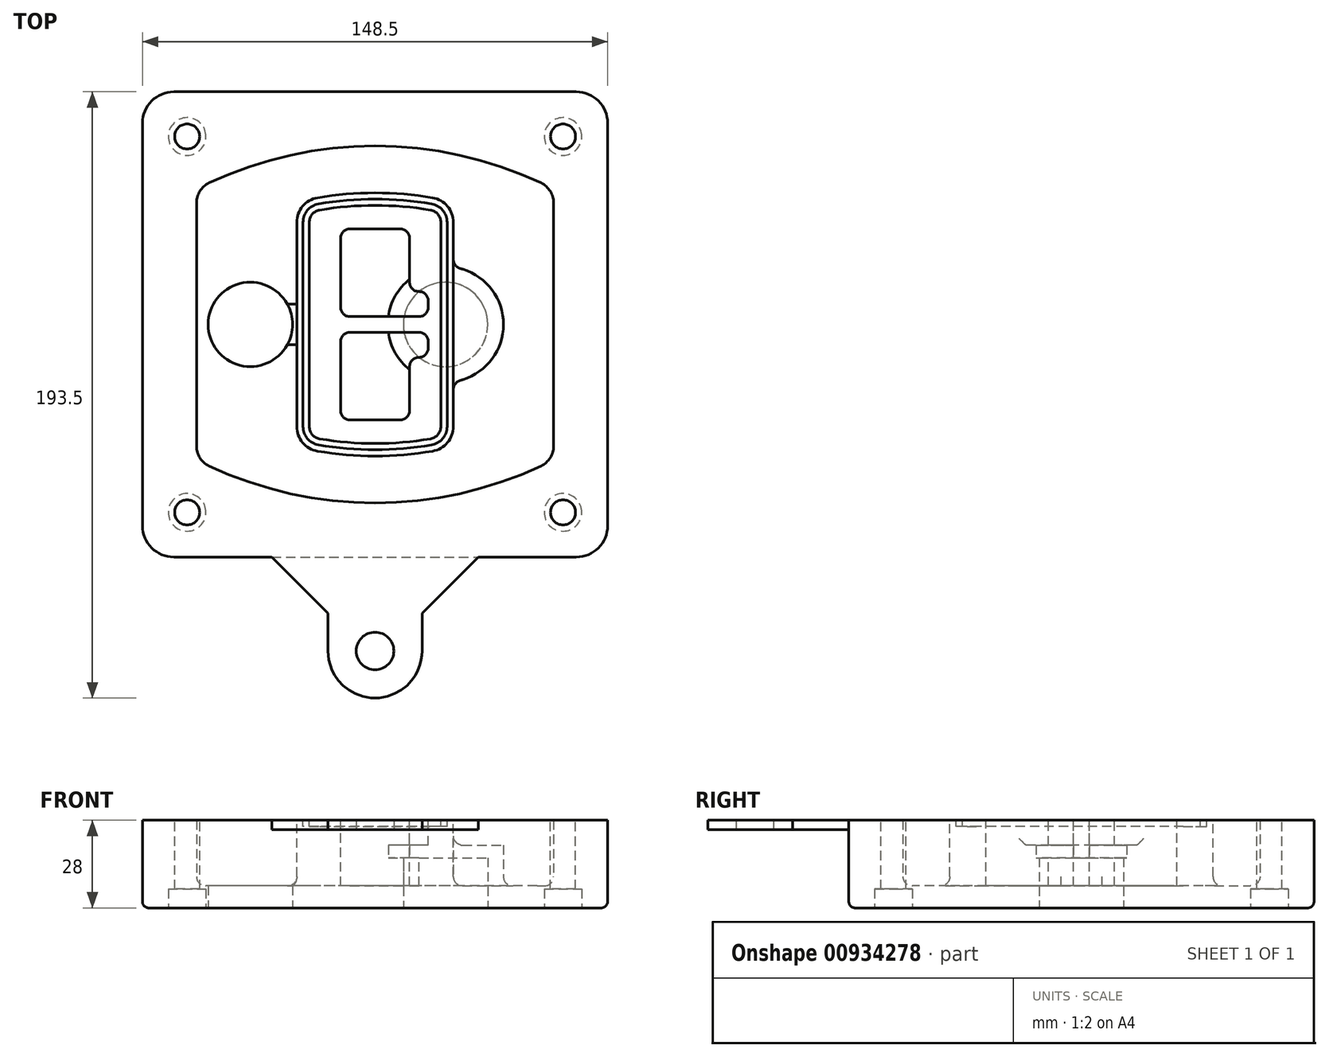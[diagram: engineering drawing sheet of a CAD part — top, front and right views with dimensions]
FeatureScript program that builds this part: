
annotation { "Feature Type Name" : "Feature", "Feature Type Description" : "" }
export const myFeature = defineFeature(function(context is Context, id is Id, definition is map)
    precondition{}
    {
        {
            var Q0;
            Q0=qCreatedBy(makeId("Top.planeOp"),FACE);
            var sketch = newSketch(context, id + "F0", { "sketchPlane" : qUnion([Q0])});
            skPoint(sketch, "E0.rect.middle", {"position": v(0, 0) * mm});
            skLineSegment(sketch, "E1.bottom", {"start": v(-64.25, -74.25) * mm, "end": v(64.25, -74.25) * mm});
            skLineSegment(sketch, "E1.top", {"start": v(-64.25, 74.25) * mm, "end": v(64.25, 74.25) * mm});
            skLineSegment(sketch, "E1.left", {"start": v(-74.25, -64.25) * mm, "end": v(-74.25, 64.25) * mm});
            skLineSegment(sketch, "E1.right", {"start": v(74.25, -64.25) * mm, "end": v(74.25, 64.25) * mm});
            skLineSegment(sketch, "E2", {"start": v(-74.25, 74.25) * mm, "end": v(74.25, -74.25) * mm, "construction": true});
            skLineSegment(sketch, "E3", {"start": v(74.25, 74.25) * mm, "end": v(-74.25, -74.25) * mm, "construction": true});
            skCircle(sketch, "E4", {"center": v(-60, 60) * mm, "radius": 4 * mm});
            skCircle(sketch, "E5", {"center": v(60, 60) * mm, "radius": 4 * mm});
            skCircle(sketch, "E6", {"center": v(60, -60) * mm, "radius": 4 * mm});
            skCircle(sketch, "E7", {"center": v(-60, -60) * mm, "radius": 4 * mm});
            skLineSegment(sketch, "E8", {"start": v(-60, 60) * mm, "end": v(60, 60) * mm, "construction": true});
            skLineSegment(sketch, "E9", {"start": v(60, 60) * mm, "end": v(60, -60) * mm, "construction": true});
            skLineSegment(sketch, "E10", {"start": v(60, -60) * mm, "end": v(-60, -60) * mm, "construction": true});
            skLineSegment(sketch, "E11", {"start": v(-60, -60) * mm, "end": v(-60, 60) * mm, "construction": true});
            skLineSegment(sketch, "E12", {"start": v(-60, 38.83) * mm, "end": v(-60, -38.83) * mm});
            skLineSegment(sketch, "E13", {"start": v(60, 38.83) * mm, "end": v(60, -38.83) * mm});
            skArc(sketch, "E14", {"start": v(54.26, 47.88) * mm, "mid": v(0, 60) * mm, "end": v(-54.26, 47.88) * mm});
            skArc(sketch, "E15", {"start": v(-54.26, -47.88) * mm, "mid": v(0, -60) * mm, "end": v(54.26, -47.88) * mm});
            skLineSegment(sketch, "E16", {"start": v(-60, 0) * mm, "end": v(60, 0) * mm, "construction": true});
            skPoint(sketch, "E17.visualSharp", {"position": v(-60, -45) * mm});
            skArc(sketch, "E17.filletArc", {"start": v(-60, -38.83) * mm, "mid": v(-58.44, -44.2) * mm, "end": v(-54.26, -47.88) * mm});
            skPoint(sketch, "E18.visualSharp", {"position": v(-60, 45) * mm});
            skArc(sketch, "E18.filletArc", {"start": v(-54.26, 47.88) * mm, "mid": v(-58.44, 44.2) * mm, "end": v(-60, 38.83) * mm});
            skPoint(sketch, "E19.visualSharp", {"position": v(60, 45) * mm});
            skArc(sketch, "E19.filletArc", {"start": v(60, 38.83) * mm, "mid": v(58.44, 44.2) * mm, "end": v(54.26, 47.88) * mm});
            skPoint(sketch, "E20.visualSharp", {"position": v(60, -45) * mm});
            skArc(sketch, "E20.filletArc", {"start": v(54.26, -47.88) * mm, "mid": v(58.44, -44.2) * mm, "end": v(60, -38.83) * mm});
            skPoint(sketch, "E21.visualSharp", {"position": v(-74.25, 74.25) * mm});
            skArc(sketch, "E21.filletArc", {"start": v(-64.25, 74.25) * mm, "mid": v(-71.32, 71.32) * mm, "end": v(-74.25, 64.25) * mm});
            skPoint(sketch, "E22.visualSharp", {"position": v(74.25, 74.25) * mm});
            skArc(sketch, "E22.filletArc", {"start": v(74.25, 64.25) * mm, "mid": v(71.32, 71.32) * mm, "end": v(64.25, 74.25) * mm});
            skPoint(sketch, "E23.visualSharp", {"position": v(74.25, -74.25) * mm});
            skArc(sketch, "E23.filletArc", {"start": v(64.25, -74.25) * mm, "mid": v(71.32, -71.32) * mm, "end": v(74.25, -64.25) * mm});
            skPoint(sketch, "E24.visualSharp", {"position": v(-74.25, -74.25) * mm});
            skArc(sketch, "E24.filletArc", {"start": v(-74.25, -64.25) * mm, "mid": v(-71.32, -71.32) * mm, "end": v(-64.25, -74.25) * mm});
            skArc(sketch, "E25.0", {"start": v(57, 38.83) * mm, "mid": v(55.9, 42.58) * mm, "end": v(52.98, 45.17) * mm});
            skLineSegment(sketch, "E25.1", {"start": v(57, 38.83) * mm, "end": v(57, -38.83) * mm});
            skArc(sketch, "E25.2", {"start": v(52.98, -45.17) * mm, "mid": v(55.9, -42.58) * mm, "end": v(57, -38.83) * mm});
            skArc(sketch, "E25.3", {"start": v(-52.98, -45.17) * mm, "mid": v(0, -57) * mm, "end": v(52.98, -45.17) * mm});
            skArc(sketch, "E25.4", {"start": v(-57, -38.83) * mm, "mid": v(-55.9, -42.58) * mm, "end": v(-52.98, -45.17) * mm});
            skArc(sketch, "E25.5", {"start": v(52.98, 45.17) * mm, "mid": v(0, 57) * mm, "end": v(-52.98, 45.17) * mm});
            skLineSegment(sketch, "E25.6", {"start": v(-57, 38.83) * mm, "end": v(-57, -38.83) * mm});
            skArc(sketch, "E25.7", {"start": v(-52.98, 45.17) * mm, "mid": v(-55.9, 42.58) * mm, "end": v(-57, 38.83) * mm});
            skArc(sketch, "E26.0", {"start": v(-55.96, 51.5) * mm, "mid": v(-61.82, 46.33) * mm, "end": v(-64, 38.83) * mm});
            skArc(sketch, "E26.1", {"start": v(55.96, 51.5) * mm, "mid": v(0, 64) * mm, "end": v(-55.96, 51.5) * mm});
            skArc(sketch, "E26.2", {"start": v(64, 38.83) * mm, "mid": v(61.82, 46.33) * mm, "end": v(55.96, 51.5) * mm});
            skLineSegment(sketch, "E26.3", {"start": v(64, 38.83) * mm, "end": v(64, -38.83) * mm});
            skArc(sketch, "E26.4", {"start": v(55.96, -51.5) * mm, "mid": v(61.82, -46.33) * mm, "end": v(64, -38.83) * mm});
            skLineSegment(sketch, "E26.5", {"start": v(-64, 38.83) * mm, "end": v(-64, -38.83) * mm});
            skArc(sketch, "E26.6", {"start": v(-55.96, -51.5) * mm, "mid": v(0, -64) * mm, "end": v(55.96, -51.5) * mm});
            skArc(sketch, "E26.7", {"start": v(-64, -38.83) * mm, "mid": v(-61.82, -46.33) * mm, "end": v(-55.96, -51.5) * mm});
            skSolve(sketch);
        }
        {
            var Q0;
            Q0=makeQuery(id+"F0.imprint","IMPRINT",FACE,{"disambiguationData":[TD([[makeQuery(id+"F0.imprint","IMPRINT",EDGE,{"derivedFrom":sQuery(id+"F0.wireOp",EDGE,"E1.bottom")}),1.0]])]});
            var Q1;
            Q1=makeQuery(id+"F0.imprint","IMPRINT",FACE,{"disambiguationData":[TD([[makeQuery(id+"F0.imprint","IMPRINT",EDGE,{"derivedFrom":sQuery(id+"F0.wireOp",EDGE,"E12")}),1.0]])]});
            var Q2;
            Q2=makeQuery(id+"F0.imprint","IMPRINT",FACE,{"disambiguationData":[TD([[makeQuery(id+"F0.imprint","IMPRINT",EDGE,{"derivedFrom":sQuery(id+"F0.wireOp",EDGE,"E25.0")}),1.0]])]});
            var Q3;
            Q3=makeQuery(id+"F0.imprint","IMPRINT",FACE,{"disambiguationData":[TD([[makeQuery(id+"F0.imprint","IMPRINT",EDGE,{"derivedFrom":sQuery(id+"F0.wireOp",EDGE,"E12")}),-1.0]])]});
            extrude(context, id + "F1", {"entities" : qUnion([Q0, Q1, Q2, Q3]), "oppositeDirection" : true, "depth" : 25 * mm});
        }
        {
            var Q0;
            Q0=makeQuery(id+"F0.imprint","IMPRINT",FACE,{"disambiguationData":[TD([[makeQuery(id+"F0.imprint","IMPRINT",EDGE,{"derivedFrom":sQuery(id+"F0.wireOp",EDGE,"E12")}),1.0]])]});
            extrude(context, id + "F2", {"entities" : qUnion([Q0]), "operationType" : NewBodyOperationType.ADD, "depth" : 3 * mm});
        }
        {
            var Q0;
            Q0=makeQuery(id+"F0.imprint","IMPRINT",FACE,{"disambiguationData":[TD([[makeQuery(id+"F0.imprint","IMPRINT",EDGE,{"derivedFrom":sQuery(id+"F0.wireOp",EDGE,"E25.0")}),1.0]])]});
            extrude(context, id + "F3", {"entities" : qUnion([Q0]), "operationType" : NewBodyOperationType.REMOVE, "oppositeDirection" : true, "depth" : 18 * mm});
        }
        {
            var Q0;
            Q0=makeQuery(id+"F2.opExtrude","CAP_FACE",FACE,{"disambiguationData":[OSD([sQuery(id+"F0.wireOp",EDGE,"E12"),sQuery(id+"F0.wireOp",EDGE,"E13"),sQuery(id+"F0.wireOp",EDGE,"E14"),sQuery(id+"F0.wireOp",EDGE,"E15"),sQuery(id+"F0.wireOp",EDGE,"E17.filletArc"),sQuery(id+"F0.wireOp",EDGE,"E18.filletArc"),sQuery(id+"F0.wireOp",EDGE,"E19.filletArc"),sQuery(id+"F0.wireOp",EDGE,"E20.filletArc"),sQuery(id+"F0.wireOp",EDGE,"E25.0"),sQuery(id+"F0.wireOp",EDGE,"E25.1"),sQuery(id+"F0.wireOp",EDGE,"E25.2"),sQuery(id+"F0.wireOp",EDGE,"E25.3"),sQuery(id+"F0.wireOp",EDGE,"E25.4"),sQuery(id+"F0.wireOp",EDGE,"E25.5"),sQuery(id+"F0.wireOp",EDGE,"E25.6"),sQuery(id+"F0.wireOp",EDGE,"E25.7")])],"isStart":false});
            var sketch = newSketch(context, id + "F4", { "sketchPlane" : qUnion([Q0])});
            skArc(sketch, "E27.0", {"start": v(-18.34, -40.45) * mm, "mid": v(0, -42) * mm, "end": v(18.34, -40.45) * mm});
            skArc(sketch, "E28.0", {"start": v(18.34, 40.45) * mm, "mid": v(0, 42) * mm, "end": v(-18.34, 40.45) * mm});
            skLineSegment(sketch, "E29", {"start": v(-25, 32.57) * mm, "end": v(-25, -32.57) * mm});
            skLineSegment(sketch, "E30", {"start": v(25, 32.57) * mm, "end": v(25, -32.57) * mm});
            skLineSegment(sketch, "E31", {"start": v(-25, 39.1) * mm, "end": v(25, 39.1) * mm, "construction": true});
            skLineSegment(sketch, "E32", {"start": v(-25, -39.1) * mm, "end": v(25, -39.1) * mm, "construction": true});
            skPoint(sketch, "E33.visualSharp", {"position": v(-25, 39.1) * mm});
            skArc(sketch, "E33.filletArc", {"start": v(-18.34, 40.45) * mm, "mid": v(-23.11, 37.73) * mm, "end": v(-25, 32.57) * mm});
            skPoint(sketch, "E34.visualSharp", {"position": v(25, 39.1) * mm});
            skArc(sketch, "E34.filletArc", {"start": v(25, 32.57) * mm, "mid": v(23.11, 37.73) * mm, "end": v(18.34, 40.45) * mm});
            skPoint(sketch, "E35.visualSharp", {"position": v(25, -39.1) * mm});
            skArc(sketch, "E35.filletArc", {"start": v(18.34, -40.45) * mm, "mid": v(23.11, -37.73) * mm, "end": v(25, -32.57) * mm});
            skPoint(sketch, "E36.visualSharp", {"position": v(-25, -39.1) * mm});
            skArc(sketch, "E36.filletArc", {"start": v(-25, -32.57) * mm, "mid": v(-23.11, -37.73) * mm, "end": v(-18.34, -40.45) * mm});
            skArc(sketch, "E37.0", {"start": v(52.98, 45.17) * mm, "mid": v(0, 57) * mm, "end": v(-52.98, 45.17) * mm});
            skArc(sketch, "E37.1", {"start": v(-52.98, 45.17) * mm, "mid": v(-55.9, 42.58) * mm, "end": v(-57, 38.83) * mm});
            skLineSegment(sketch, "E37.2", {"start": v(-57, 38.83) * mm, "end": v(-57, -38.83) * mm});
            skArc(sketch, "E37.3", {"start": v(-57, -38.83) * mm, "mid": v(-55.9, -42.58) * mm, "end": v(-52.98, -45.17) * mm});
            skArc(sketch, "E37.4", {"start": v(-52.98, -45.17) * mm, "mid": v(0, -57) * mm, "end": v(52.98, -45.17) * mm});
            skArc(sketch, "E37.5", {"start": v(52.98, -45.17) * mm, "mid": v(55.9, -42.58) * mm, "end": v(57, -38.83) * mm});
            skLineSegment(sketch, "E37.6", {"start": v(57, 38.83) * mm, "end": v(57, -38.83) * mm});
            skArc(sketch, "E37.7", {"start": v(57, 38.83) * mm, "mid": v(55.9, 42.58) * mm, "end": v(52.98, 45.17) * mm});
            skLineSegment(sketch, "E38.0", {"start": v(23, 32.57) * mm, "end": v(23, -32.57) * mm});
            skArc(sketch, "E38.1", {"start": v(18, -38.48) * mm, "mid": v(21.58, -36.44) * mm, "end": v(23, -32.57) * mm});
            skArc(sketch, "E38.2", {"start": v(-18, -38.48) * mm, "mid": v(0, -40) * mm, "end": v(18, -38.48) * mm});
            skArc(sketch, "E38.3", {"start": v(-23, -32.57) * mm, "mid": v(-21.58, -36.44) * mm, "end": v(-18, -38.48) * mm});
            skLineSegment(sketch, "E38.4", {"start": v(-23, 32.57) * mm, "end": v(-23, -32.57) * mm});
            skArc(sketch, "E38.5", {"start": v(23, 32.57) * mm, "mid": v(21.58, 36.44) * mm, "end": v(18, 38.48) * mm});
            skArc(sketch, "E38.6", {"start": v(-18, 38.48) * mm, "mid": v(-21.58, 36.44) * mm, "end": v(-23, 32.57) * mm});
            skArc(sketch, "E38.7", {"start": v(18, 38.48) * mm, "mid": v(0, 40) * mm, "end": v(-18, 38.48) * mm});
            skArc(sketch, "E39.0", {"start": v(21, 32.57) * mm, "mid": v(20.06, 35.15) * mm, "end": v(17.67, 36.5) * mm});
            skLineSegment(sketch, "E39.1", {"start": v(21, 32.57) * mm, "end": v(21, -32.57) * mm});
            skArc(sketch, "E39.2", {"start": v(17.67, -36.5) * mm, "mid": v(20.06, -35.15) * mm, "end": v(21, -32.57) * mm});
            skArc(sketch, "E39.3", {"start": v(-17.67, -36.5) * mm, "mid": v(0, -38) * mm, "end": v(17.67, -36.5) * mm});
            skArc(sketch, "E39.4", {"start": v(-21, -32.57) * mm, "mid": v(-20.06, -35.15) * mm, "end": v(-17.67, -36.5) * mm});
            skArc(sketch, "E39.5", {"start": v(17.67, 36.5) * mm, "mid": v(0, 38) * mm, "end": v(-17.67, 36.5) * mm});
            skLineSegment(sketch, "E39.6", {"start": v(-21, 32.57) * mm, "end": v(-21, -32.57) * mm});
            skArc(sketch, "E39.7", {"start": v(-17.67, 36.5) * mm, "mid": v(-20.06, 35.15) * mm, "end": v(-21, 32.57) * mm});
            skLineSegment(sketch, "E40", {"start": v(-25, 0) * mm, "end": v(25, 0) * mm, "construction": true});
            skLineSegment(sketch, "E41", {"start": v(-11, 5.5) * mm, "end": v(-11, 27.5) * mm});
            skLineSegment(sketch, "E42", {"start": v(-8, 30.5) * mm, "end": v(8, 30.5) * mm});
            skLineSegment(sketch, "E43", {"start": v(11, 27.5) * mm, "end": v(11, 13.5) * mm});
            skLineSegment(sketch, "E44", {"start": v(14, 10.5) * mm, "end": v(14, 10.5) * mm});
            skLineSegment(sketch, "E45", {"start": v(17, 7.5) * mm, "end": v(17, 5.5) * mm});
            skLineSegment(sketch, "E46", {"start": v(14, 2.5) * mm, "end": v(-8, 2.5) * mm});
            skPoint(sketch, "E47.visualSharp", {"position": v(-11, 30.5) * mm});
            skArc(sketch, "E47.filletArc", {"start": v(-8, 30.5) * mm, "mid": v(-10.12, 29.62) * mm, "end": v(-11, 27.5) * mm});
            skPoint(sketch, "E48.visualSharp", {"position": v(11, 30.5) * mm});
            skArc(sketch, "E48.filletArc", {"start": v(11, 27.5) * mm, "mid": v(10.12, 29.62) * mm, "end": v(8, 30.5) * mm});
            skPoint(sketch, "E49.visualSharp", {"position": v(11, 10.5) * mm});
            skArc(sketch, "E49.filletArc", {"start": v(11, 13.5) * mm, "mid": v(11.88, 11.38) * mm, "end": v(14, 10.5) * mm});
            skPoint(sketch, "E50.visualSharp", {"position": v(17, 10.5) * mm});
            skArc(sketch, "E50.filletArc", {"start": v(17, 7.5) * mm, "mid": v(16.12, 9.62) * mm, "end": v(14, 10.5) * mm});
            skPoint(sketch, "E51.visualSharp", {"position": v(17, 2.5) * mm});
            skArc(sketch, "E51.filletArc", {"start": v(14, 2.5) * mm, "mid": v(16.12, 3.38) * mm, "end": v(17, 5.5) * mm});
            skPoint(sketch, "E52.visualSharp", {"position": v(-11, 2.5) * mm});
            skArc(sketch, "E52.filletArc", {"start": v(-11, 5.5) * mm, "mid": v(-10.12, 3.38) * mm, "end": v(-8, 2.5) * mm});
            skLineSegment(sketch, "E53.0.MirrorCS", {"start": v(14, -2.5) * mm, "end": v(-8, -2.5) * mm});
            skArc(sketch, "E54.0.MirrorCS", {"start": v(-11, -5.5) * mm, "mid": v(-10.12, -3.38) * mm, "end": v(-8, -2.5) * mm});
            skLineSegment(sketch, "E55.0.MirrorCS", {"start": v(-11, -5.5) * mm, "end": v(-11, -27.5) * mm});
            skArc(sketch, "E56.0.MirrorCS", {"start": v(-8, -30.5) * mm, "mid": v(-10.12, -29.62) * mm, "end": v(-11, -27.5) * mm});
            skLineSegment(sketch, "E57.0.MirrorCS", {"start": v(-8, -30.5) * mm, "end": v(8, -30.5) * mm});
            skArc(sketch, "E58.0.MirrorCS", {"start": v(11, -27.5) * mm, "mid": v(10.12, -29.62) * mm, "end": v(8, -30.5) * mm});
            skLineSegment(sketch, "E59.0.MirrorCS", {"start": v(11, -27.5) * mm, "end": v(11, -13.5) * mm});
            skArc(sketch, "E60.0.MirrorCS", {"start": v(11, -13.5) * mm, "mid": v(11.88, -11.38) * mm, "end": v(14, -10.5) * mm});
            skArc(sketch, "E61.0.MirrorCS", {"start": v(17, -7.5) * mm, "mid": v(16.12, -9.62) * mm, "end": v(14, -10.5) * mm});
            skLineSegment(sketch, "E62.0.MirrorCS", {"start": v(17, -7.5) * mm, "end": v(17, -5.5) * mm});
            skArc(sketch, "E63.0.MirrorCS", {"start": v(14, -2.5) * mm, "mid": v(16.12, -3.38) * mm, "end": v(17, -5.5) * mm});
            skSolve(sketch);
        }
        {
            var Q0;
            Q0=makeQuery(id+"F4.imprint","IMPRINT",FACE,{"disambiguationData":[TD([[makeQuery(id+"F4.imprint","IMPRINT",EDGE,{"derivedFrom":sQuery(id+"F4.wireOp",EDGE,"E27.0")}),1.0]])]});
            var Q1;
            Q1=makeQuery(id+"F4.imprint","IMPRINT",FACE,{"disambiguationData":[TD([[makeQuery(id+"F4.imprint","IMPRINT",EDGE,{"derivedFrom":sQuery(id+"F4.wireOp",EDGE,"E38.0")}),-1.0]])]});
            var Q2;
            Q2=makeQuery(id+"F4.imprint","IMPRINT",FACE,{"disambiguationData":[TD([[makeQuery(id+"F4.imprint","IMPRINT",EDGE,{"derivedFrom":sQuery(id+"F4.wireOp",EDGE,"E39.0")}),1.0]])]});
            extrude(context, id + "F5", {"entities" : qUnion([Q0, Q1, Q2]), "operationType" : NewBodyOperationType.ADD, "endBound" : BoundingType.UP_TO_NEXT, "oppositeDirection" : true, "depth" : 25 * mm});
        }
        {
            var Q0;
            Q0=makeQuery(id+"F4.imprint","IMPRINT",FACE,{"disambiguationData":[TD([[makeQuery(id+"F4.imprint","IMPRINT",EDGE,{"derivedFrom":sQuery(id+"F4.wireOp",EDGE,"E38.0")}),-1.0]])]});
            extrude(context, id + "F6", {"entities" : qUnion([Q0]), "operationType" : NewBodyOperationType.REMOVE, "oppositeDirection" : true, "depth" : 2 * mm});
        }
        {
            var Q0;
            Q0=makeQuery(id+"F1.opExtrude","CAP_FACE",FACE,{"disambiguationData":[OSD([sQuery(id+"F0.wireOp",EDGE,"E1.bottom"),sQuery(id+"F0.wireOp",EDGE,"E1.top"),sQuery(id+"F0.wireOp",EDGE,"E1.left"),sQuery(id+"F0.wireOp",EDGE,"E1.right"),sQuery(id+"F0.wireOp",EDGE,"E4"),sQuery(id+"F0.wireOp",EDGE,"E5"),sQuery(id+"F0.wireOp",EDGE,"E6"),sQuery(id+"F0.wireOp",EDGE,"E7"),sQuery(id+"F0.wireOp",EDGE,"E21.filletArc"),sQuery(id+"F0.wireOp",EDGE,"E22.filletArc"),sQuery(id+"F0.wireOp",EDGE,"E23.filletArc"),sQuery(id+"F0.wireOp",EDGE,"E24.filletArc")])],"isStart":false});
            var sketch = newSketch(context, id + "F7", { "sketchPlane" : qUnion([Q0])});
            skCircle(sketch, "E64", {"center": v(22.5, 0) * mm, "radius": 13.47 * mm});
            skCircle(sketch, "E65", {"center": v(-39.81, 0) * mm, "radius": 13.47 * mm});
            skLineSegment(sketch, "E66", {"start": v(74.25, 0) * mm, "end": v(-74.25, 0) * mm});
            skCircle(sketch, "E67", {"center": v(22.5, 0) * mm, "radius": 18.47 * mm});
            skCircle(sketch, "E68", {"center": v(60, -60) * mm, "radius": 6 * mm});
            skCircle(sketch, "E69", {"center": v(-60, -60) * mm, "radius": 6 * mm});
            skCircle(sketch, "E70", {"center": v(-60, 60) * mm, "radius": 6 * mm});
            skCircle(sketch, "E71", {"center": v(60, 60) * mm, "radius": 6 * mm});
            skSolve(sketch);
        }
        {
            var Q0;
            {var subQ1=sQuery(id+"F7.wireOp",EDGE,"E66");var subQ4=sQuery(id+"F7.wireOp",EDGE,"E64");var subQ6=makeQuery(id+"F7.imprint","INTERSECT",VERTEX,{"disambiguationData":[OD(0.0)],"derivedFrom":[subQ4,subQ1]});Q0=makeQuery(id+"F7.imprint","IMPRINT",FACE,{"disambiguationData":[TD([[makeQuery(id+"F7.imprint","IMPRINT",EDGE,{"disambiguationData":[TD([[subQ6,-1.0]])],"derivedFrom":subQ4}),-1.0]])]});}
            var Q1;
            {var subQ0=sQuery(id+"F7.wireOp",EDGE,"E66");var subQ1=sQuery(id+"F7.wireOp",EDGE,"E64");var subQ3=makeQuery(id+"F7.imprint","INTERSECT",VERTEX,{"disambiguationData":[OD(0.0)],"derivedFrom":[subQ1,subQ0]});Q1=makeQuery(id+"F7.imprint","IMPRINT",FACE,{"disambiguationData":[TD([[makeQuery(id+"F7.imprint","IMPRINT",EDGE,{"disambiguationData":[TD([[subQ3,-1.0]])],"derivedFrom":subQ1}),1.0]])]});}
            var Q2;
            {var subQ0=sQuery(id+"F7.wireOp",EDGE,"E66");var subQ1=sQuery(id+"F7.wireOp",EDGE,"E64");var subQ3=makeQuery(id+"F7.imprint","INTERSECT",VERTEX,{"disambiguationData":[OD(0.0)],"derivedFrom":[subQ1,subQ0]});Q2=makeQuery(id+"F7.imprint","IMPRINT",FACE,{"disambiguationData":[TD([[makeQuery(id+"F7.imprint","IMPRINT",EDGE,{"disambiguationData":[TD([[subQ3,1.0]])],"derivedFrom":subQ1}),1.0]])]});}
            var Q3;
            {var subQ1=sQuery(id+"F7.wireOp",EDGE,"E66");var subQ4=sQuery(id+"F7.wireOp",EDGE,"E64");var subQ6=makeQuery(id+"F7.imprint","INTERSECT",VERTEX,{"disambiguationData":[OD(0.0)],"derivedFrom":[subQ4,subQ1]});Q3=makeQuery(id+"F7.imprint","IMPRINT",FACE,{"disambiguationData":[TD([[makeQuery(id+"F7.imprint","IMPRINT",EDGE,{"disambiguationData":[TD([[subQ6,1.0]])],"derivedFrom":subQ4}),-1.0]])]});}
            extrude(context, id + "F8", {"entities" : qUnion([Q0, Q1, Q2, Q3]), "operationType" : NewBodyOperationType.ADD, "oppositeDirection" : true, "depth" : 20 * mm});
        }
        {
            var Q0;
            {var subQ0=sQuery(id+"F7.wireOp",EDGE,"E66");var subQ1=sQuery(id+"F7.wireOp",EDGE,"E64");var subQ3=makeQuery(id+"F7.imprint","INTERSECT",VERTEX,{"disambiguationData":[OD(0.0)],"derivedFrom":[subQ1,subQ0]});Q0=makeQuery(id+"F7.imprint","IMPRINT",FACE,{"disambiguationData":[TD([[makeQuery(id+"F7.imprint","IMPRINT",EDGE,{"disambiguationData":[TD([[subQ3,-1.0]])],"derivedFrom":subQ1}),1.0]])]});}
            var Q1;
            {var subQ0=sQuery(id+"F7.wireOp",EDGE,"E66");var subQ1=sQuery(id+"F7.wireOp",EDGE,"E64");var subQ3=makeQuery(id+"F7.imprint","INTERSECT",VERTEX,{"disambiguationData":[OD(0.0)],"derivedFrom":[subQ1,subQ0]});Q1=makeQuery(id+"F7.imprint","IMPRINT",FACE,{"disambiguationData":[TD([[makeQuery(id+"F7.imprint","IMPRINT",EDGE,{"disambiguationData":[TD([[subQ3,1.0]])],"derivedFrom":subQ1}),1.0]])]});}
            extrude(context, id + "F9", {"entities" : qUnion([Q0, Q1]), "operationType" : NewBodyOperationType.REMOVE, "oppositeDirection" : true, "depth" : 16 * mm});
        }
        {
            var Q0;
            {var subQ0=sQuery(id+"F7.wireOp",EDGE,"E66");var subQ1=sQuery(id+"F7.wireOp",EDGE,"E65");var subQ3=makeQuery(id+"F7.imprint","INTERSECT",VERTEX,{"disambiguationData":[OD(0.0)],"derivedFrom":[subQ1,subQ0]});Q0=makeQuery(id+"F7.imprint","IMPRINT",FACE,{"disambiguationData":[TD([[makeQuery(id+"F7.imprint","IMPRINT",EDGE,{"disambiguationData":[TD([[subQ3,-1.0]])],"derivedFrom":subQ1}),1.0]])]});}
            var Q1;
            {var subQ0=sQuery(id+"F7.wireOp",EDGE,"E66");var subQ1=sQuery(id+"F7.wireOp",EDGE,"E65");var subQ3=makeQuery(id+"F7.imprint","INTERSECT",VERTEX,{"disambiguationData":[OD(0.0)],"derivedFrom":[subQ1,subQ0]});Q1=makeQuery(id+"F7.imprint","IMPRINT",FACE,{"disambiguationData":[TD([[makeQuery(id+"F7.imprint","IMPRINT",EDGE,{"disambiguationData":[TD([[subQ3,1.0]])],"derivedFrom":subQ1}),1.0]])]});}
            extrude(context, id + "F10", {"entities" : qUnion([Q0, Q1]), "operationType" : NewBodyOperationType.REMOVE, "oppositeDirection" : true, "depth" : 25 * mm});
        }
        {
            var Q0;
            Q0=makeQuery(id+"F7.imprint","IMPRINT",FACE,{"disambiguationData":[TD([[makeQuery(id+"F7.imprint","IMPRINT",EDGE,{"derivedFrom":sQuery(id+"F7.wireOp",EDGE,"E68")}),1.0]])]});
            var Q1;
            Q1=makeQuery(id+"F7.imprint","IMPRINT",FACE,{"disambiguationData":[TD([[makeQuery(id+"F7.imprint","IMPRINT",EDGE,{"derivedFrom":makeQuery(id+"F1.opExtrude","CAP_EDGE",EDGE,{"disambiguationData":[OSD([sQuery(id+"F0.wireOp",EDGE,"E5")])],"isStart":false})}),-1.0]])]});
            var Q2;
            Q2=makeQuery(id+"F7.imprint","IMPRINT",FACE,{"disambiguationData":[TD([[makeQuery(id+"F7.imprint","IMPRINT",EDGE,{"derivedFrom":sQuery(id+"F7.wireOp",EDGE,"E69")}),1.0]])]});
            var Q3;
            Q3=makeQuery(id+"F7.imprint","IMPRINT",FACE,{"disambiguationData":[TD([[makeQuery(id+"F7.imprint","IMPRINT",EDGE,{"derivedFrom":makeQuery(id+"F1.opExtrude","CAP_EDGE",EDGE,{"disambiguationData":[OSD([sQuery(id+"F0.wireOp",EDGE,"E4")])],"isStart":false})}),-1.0]])]});
            var Q4;
            Q4=makeQuery(id+"F7.imprint","IMPRINT",FACE,{"disambiguationData":[TD([[makeQuery(id+"F7.imprint","IMPRINT",EDGE,{"derivedFrom":sQuery(id+"F7.wireOp",EDGE,"E70")}),1.0]])]});
            var Q5;
            Q5=makeQuery(id+"F7.imprint","IMPRINT",FACE,{"disambiguationData":[TD([[makeQuery(id+"F7.imprint","IMPRINT",EDGE,{"derivedFrom":makeQuery(id+"F1.opExtrude","CAP_EDGE",EDGE,{"disambiguationData":[OSD([sQuery(id+"F0.wireOp",EDGE,"E7")])],"isStart":false})}),-1.0]])]});
            var Q6;
            Q6=makeQuery(id+"F7.imprint","IMPRINT",FACE,{"disambiguationData":[TD([[makeQuery(id+"F7.imprint","IMPRINT",EDGE,{"derivedFrom":sQuery(id+"F7.wireOp",EDGE,"E71")}),1.0]])]});
            var Q7;
            Q7=makeQuery(id+"F7.imprint","IMPRINT",FACE,{"disambiguationData":[TD([[makeQuery(id+"F7.imprint","IMPRINT",EDGE,{"derivedFrom":makeQuery(id+"F1.opExtrude","CAP_EDGE",EDGE,{"disambiguationData":[OSD([sQuery(id+"F0.wireOp",EDGE,"E6")])],"isStart":false})}),-1.0]])]});
            extrude(context, id + "F11", {"entities" : qUnion([Q0, Q1, Q2, Q3, Q4, Q5, Q6, Q7]), "operationType" : NewBodyOperationType.REMOVE, "oppositeDirection" : true, "depth" : 6 * mm});
        }
        {
            var Q0;
            Q0=makeQuery(id+"F9.boolean.opBoolean","COPY",FACE,{"derivedFrom":makeQuery(id+"F9.opExtrude","CAP_FACE",FACE,{"disambiguationData":[OSD([sQuery(id+"F7.wireOp",EDGE,"E64")])],"isStart":false})});
            var sketch = newSketch(context, id + "F12", { "sketchPlane" : qUnion([Q0])});
            skArc(sketch, "E72.0", {"start": v(11, 14.45) * mm, "mid": v(6.45, 9.13) * mm, "end": v(4.2, 2.5) * mm});
            skArc(sketch, "E72.1", {"start": v(4.2, -2.5) * mm, "mid": v(6.45, -9.13) * mm, "end": v(11, -14.45) * mm});
            skLineSegment(sketch, "E73", {"start": v(4.2, -2.5) * mm, "end": v(14, -2.5) * mm});
            skLineSegment(sketch, "E74.0", {"start": v(14, 2.5) * mm, "end": v(4.2, 2.5) * mm});
            skArc(sketch, "E74.1", {"start": v(14, 2.5) * mm, "mid": v(16.12, 3.38) * mm, "end": v(17, 5.5) * mm});
            skLineSegment(sketch, "E74.2", {"start": v(17, 7.5) * mm, "end": v(17, 5.5) * mm});
            skArc(sketch, "E74.3", {"start": v(17, 7.5) * mm, "mid": v(16.12, 9.62) * mm, "end": v(14, 10.5) * mm});
            skArc(sketch, "E74.4", {"start": v(11, 13.5) * mm, "mid": v(11.88, 11.38) * mm, "end": v(14, 10.5) * mm});
            skLineSegment(sketch, "E74.5", {"start": v(11, 14.45) * mm, "end": v(11, 13.5) * mm});
            skLineSegment(sketch, "E74.7", {"start": v(14, -2.5) * mm, "end": v(4.2, -2.5) * mm});
            skArc(sketch, "E74.8", {"start": v(14, -2.5) * mm, "mid": v(16.12, -3.38) * mm, "end": v(17, -5.5) * mm});
            skLineSegment(sketch, "E74.9", {"start": v(17, -7.5) * mm, "end": v(17, -5.5) * mm});
            skArc(sketch, "E74.10", {"start": v(17, -7.5) * mm, "mid": v(16.12, -9.62) * mm, "end": v(14, -10.5) * mm});
            skArc(sketch, "E74.11", {"start": v(11, -13.5) * mm, "mid": v(11.88, -11.38) * mm, "end": v(14, -10.5) * mm});
            skLineSegment(sketch, "E74.12", {"start": v(11, -14.45) * mm, "end": v(11, -13.5) * mm});
            skPoint(sketch, "E75.orphan", {"position": v(11, -27.5) * mm});
            skPoint(sketch, "E76.orphan", {"position": v(-8, -2.5) * mm});
            skPoint(sketch, "E77.orphan", {"position": v(-8, 2.5) * mm});
            skPoint(sketch, "E78.orphan", {"position": v(11, 27.5) * mm});
            skSolve(sketch);
        }
        {
            var Q0;
            {var subQ7=sQuery(id+"F12.wireOp",EDGE,"E72.0");var subQ14=sQuery(id+"F12.wireOp",EDGE,"E72.1");var subQ16=sQuery(id+"F12.wireOp",EDGE,"E74.1");var subQ18=sQuery(id+"F12.wireOp",EDGE,"E74.8");Q0=qUnion([makeQuery(id+"F12.imprint","IMPRINT",FACE,{"disambiguationData":[TD([[makeQuery(id+"F12.imprint","IMPRINT",EDGE,{"derivedFrom":subQ7}),1.0]])]}),makeQuery(id+"F12.imprint","IMPRINT",FACE,{"disambiguationData":[TD([[makeQuery(id+"F12.imprint","IMPRINT",EDGE,{"derivedFrom":subQ14}),1.0]])]}),makeQuery(id+"F12.imprint","IMPRINT",FACE,{"disambiguationData":[TD([[makeQuery(id+"F12.imprint","IMPRINT",EDGE,{"derivedFrom":subQ16}),1.0]])]}),makeQuery(id+"F12.imprint","IMPRINT",FACE,{"disambiguationData":[TD([[makeQuery(id+"F12.imprint","IMPRINT",EDGE,{"derivedFrom":subQ18}),-1.0]])]})]);}
            var Q1;
            Q1=makeQuery(id+"F5.boolean.opBoolean","SPLIT",FACE,{"disambiguationData":[TD([makeQuery(id+"F5.opExtrude","SWEPT_FACE",FACE,{"disambiguationData":[OSD([sQuery(id+"F4.wireOp",EDGE,"E41")])]})])],"derivedFrom":makeQuery(id+"F3.boolean.opBoolean","COPY",FACE,{"derivedFrom":makeQuery(id+"F3.opExtrude","CAP_FACE",FACE,{"disambiguationData":[OSD([sQuery(id+"F0.wireOp",EDGE,"E25.0"),sQuery(id+"F0.wireOp",EDGE,"E25.1"),sQuery(id+"F0.wireOp",EDGE,"E25.2"),sQuery(id+"F0.wireOp",EDGE,"E25.3"),sQuery(id+"F0.wireOp",EDGE,"E25.4"),sQuery(id+"F0.wireOp",EDGE,"E25.5"),sQuery(id+"F0.wireOp",EDGE,"E25.6"),sQuery(id+"F0.wireOp",EDGE,"E25.7")])],"isStart":false})})});
            extrude(context, id + "F13", {"entities" : qUnion([Q0]), "operationType" : NewBodyOperationType.REMOVE, "endBound" : BoundingType.UP_TO_SURFACE, "endBoundEntityFace" : qUnion([Q1]), "depth" : 25 * mm});
        }
        {
            var Q0;
            Q0=makeQuery(id+"F3.boolean.opBoolean","COPY",EDGE,{"derivedFrom":makeQuery(id+"F3.opExtrude","CAP_EDGE",EDGE,{"disambiguationData":[OSD([sQuery(id+"F0.wireOp",EDGE,"E25.6")])],"isStart":false})});
            var Q1;
            Q1=makeQuery(id+"F8.boolean.opBoolean","INTERSECT",EDGE,{"derivedFrom":[makeQuery(id+"F5.opExtrude","SWEPT_FACE",FACE,{"disambiguationData":[OSD([sQuery(id+"F4.wireOp",EDGE,"E30")])]}),makeQuery(id+"F8.opExtrude","CAP_FACE",FACE,{"disambiguationData":[OSD([sQuery(id+"F7.wireOp",EDGE,"E67")])],"isStart":false})]});
            var Q2;
            Q2=makeQuery(id+"F8.boolean.opBoolean","INTERSECT",EDGE,{"disambiguationData":[OD(1.0)],"derivedFrom":[makeQuery(id+"F5.opExtrude","SWEPT_FACE",FACE,{"disambiguationData":[OSD([sQuery(id+"F4.wireOp",EDGE,"E30")])]}),makeQuery(id+"F8.opExtrude","SWEPT_FACE",FACE,{"disambiguationData":[OSD([sQuery(id+"F7.wireOp",EDGE,"E67")])]})]});
            var Q3;
            {var subQ0=sQuery(id+"F4.wireOp",EDGE,"E30");Q3=makeQuery(id+"F8.boolean.opBoolean","SPLIT",EDGE,{"disambiguationData":[TD([makeQuery(id+"F5.opExtrude","SWEPT_FACE",FACE,{"disambiguationData":[OSD([sQuery(id+"F4.wireOp",EDGE,"E35.filletArc")])]})])],"derivedFrom":makeQuery(id+"F5.opExtrude","CAP_EDGE",EDGE,{"disambiguationData":[OSD([subQ0])],"isStart":false})});}
            var Q4;
            {var subQ0=sQuery(id+"F0.wireOp",EDGE,"E25.7");var subQ1=sQuery(id+"F0.wireOp",EDGE,"E25.1");var subQ2=sQuery(id+"F0.wireOp",EDGE,"E25.6");var subQ3=sQuery(id+"F0.wireOp",EDGE,"E25.5");var subQ4=sQuery(id+"F0.wireOp",EDGE,"E25.4");var subQ5=sQuery(id+"F0.wireOp",EDGE,"E25.0");var subQ6=sQuery(id+"F0.wireOp",EDGE,"E25.2");var subQ7=sQuery(id+"F0.wireOp",EDGE,"E25.3");Q4=makeQuery(id+"F8.boolean.opBoolean","INTERSECT",EDGE,{"derivedFrom":[makeQuery(id+"F5.boolean.opBoolean","SPLIT",FACE,{"disambiguationData":[TD([makeQuery(id+"F2.opExtrude","SWEPT_FACE",FACE,{"disambiguationData":[OSD([subQ5])]})])],"derivedFrom":makeQuery(id+"F3.boolean.opBoolean","COPY",FACE,{"derivedFrom":makeQuery(id+"F3.opExtrude","CAP_FACE",FACE,{"disambiguationData":[OSD([subQ5,subQ1,subQ6,subQ7,subQ4,subQ3,subQ2,subQ0])],"isStart":false})})}),makeQuery(id+"F8.opExtrude","SWEPT_FACE",FACE,{"disambiguationData":[OSD([sQuery(id+"F7.wireOp",EDGE,"E67")])]})]});}
            var Q5;
            Q5=makeQuery(id+"F8.boolean.opBoolean","INTERSECT",EDGE,{"disambiguationData":[OD(0.0)],"derivedFrom":[makeQuery(id+"F5.opExtrude","SWEPT_FACE",FACE,{"disambiguationData":[OSD([sQuery(id+"F4.wireOp",EDGE,"E30")])]}),makeQuery(id+"F8.opExtrude","SWEPT_FACE",FACE,{"disambiguationData":[OSD([sQuery(id+"F7.wireOp",EDGE,"E67")])]})]});
            fillet(context, id + "F14", {"entities" : qUnion([Q0, Q1, Q2, Q3, Q4, Q5]), "radius" : 3 * mm, "tangentPropagation" : true, "allowEdgeOverflow" : false});
        }
        {
            var Q0;
            Q0=makeQuery(id+"F1.opExtrude","CAP_EDGE",EDGE,{"disambiguationData":[OSD([sQuery(id+"F0.wireOp",EDGE,"E1.bottom")])],"isStart":false});
            fillet(context, id + "F15", {"entities" : qUnion([Q0]), "radius" : 2 * mm, "tangentPropagation" : true, "allowEdgeOverflow" : false});
        }
        {
            var Q0;
            {var subQ0=sQuery(id+"F0.wireOp",EDGE,"E21.filletArc");var subQ1=sQuery(id+"F0.wireOp",EDGE,"E7");var subQ2=sQuery(id+"F0.wireOp",EDGE,"E6");var subQ3=sQuery(id+"F0.wireOp",EDGE,"E5");var subQ4=sQuery(id+"F0.wireOp",EDGE,"E4");var subQ5=sQuery(id+"F0.wireOp",EDGE,"E22.filletArc");var subQ6=sQuery(id+"F0.wireOp",EDGE,"E1.bottom");var subQ7=sQuery(id+"F0.wireOp",EDGE,"E1.right");var subQ8=sQuery(id+"F0.wireOp",EDGE,"E1.top");var subQ9=sQuery(id+"F0.wireOp",EDGE,"E1.left");var subQ10=sQuery(id+"F0.wireOp",EDGE,"E23.filletArc");var subQ11=sQuery(id+"F0.wireOp",EDGE,"E24.filletArc");Q0=makeQuery(id+"F2.boolean.opBoolean","SPLIT",FACE,{"disambiguationData":[TD([makeQuery(id+"F1.opExtrude","SWEPT_FACE",FACE,{"disambiguationData":[OSD([subQ6])]})])],"derivedFrom":makeQuery(id+"F1.opExtrude","CAP_FACE",FACE,{"disambiguationData":[OSD([subQ6,subQ8,subQ9,subQ7,subQ4,subQ3,subQ2,subQ1,subQ0,subQ5,subQ10,subQ11])],"isStart":true})});}
            var sketch = newSketch(context, id + "F16", { "sketchPlane" : qUnion([Q0])});
            skCircle(sketch, "E79", {"center": v(0, 104.25) * mm, "radius": 6 * mm});
            skLineSegment(sketch, "E80", {"start": v(-15, 104.25) * mm, "end": v(-15, 92.25) * mm});
            skLineSegment(sketch, "E81", {"start": v(-33, 74.25) * mm, "end": v(-15, 92.25) * mm});
            skLineSegment(sketch, "E82", {"start": v(0, 104.25) * mm, "end": v(0, 74.25) * mm, "construction": true});
            skArc(sketch, "E83", {"start": v(15, 104.25) * mm, "mid": v(0, 119.25) * mm, "end": v(-15, 104.25) * mm});
            skLineSegment(sketch, "E84", {"start": v(15, 104.25) * mm, "end": v(15, 92.25) * mm});
            skLineSegment(sketch, "E85", {"start": v(15, 92.25) * mm, "end": v(33, 74.25) * mm});
            skLineSegment(sketch, "E86", {"start": v(-74.25, 0) * mm, "end": v(74.25, 0) * mm, "construction": true});
            skLineSegment(sketch, "E87.MirrorCS", {"start": v(33, 74.25) * mm, "end": v(15, 92.25) * mm});
            skArc(sketch, "E88.MirrorCS", {"start": v(-15, 104.25) * mm, "mid": v(0, 119.25) * mm, "end": v(15, 104.25) * mm});
            skLineSegment(sketch, "E89.MirrorCS", {"start": v(-15, 92.25) * mm, "end": v(-33, 74.25) * mm});
            skLineSegment(sketch, "E90.MirrorCS", {"start": v(74.25, 0) * mm, "end": v(-74.25, 0) * mm, "construction": true});
            skLineSegment(sketch, "E91.MirrorCS", {"start": v(33, -74.25) * mm, "end": v(15, -92.25) * mm});
            skLineSegment(sketch, "E92.MirrorCS", {"start": v(-33, -74.25) * mm, "end": v(-15, -92.25) * mm});
            skLineSegment(sketch, "E93.MirrorCS", {"start": v(15, -92.25) * mm, "end": v(33, -74.25) * mm});
            skLineSegment(sketch, "E94.MirrorCS", {"start": v(-15, -92.25) * mm, "end": v(-33, -74.25) * mm});
            skCircle(sketch, "E95.MirrorC", {"center": v(0, -104.25) * mm, "radius": 6 * mm});
            skLineSegment(sketch, "E96.MirrorCS", {"start": v(-15, -104.25) * mm, "end": v(-15, -92.25) * mm});
            skArc(sketch, "E97.MirrorCS", {"start": v(15, -104.25) * mm, "mid": v(0, -119.25) * mm, "end": v(-15, -104.25) * mm});
            skLineSegment(sketch, "E98.MirrorCS", {"start": v(15, -104.25) * mm, "end": v(15, -92.25) * mm});
            skArc(sketch, "E99.MirrorCS", {"start": v(-15, -104.25) * mm, "mid": v(0, -119.25) * mm, "end": v(15, -104.25) * mm});
            skLineSegment(sketch, "E100.MirrorCS", {"start": v(0, -104.25) * mm, "end": v(0, -74.25) * mm, "construction": true});
            skSolve(sketch);
        }
        {
            var Q0;
            {var subQ1=sQuery(id+"F16.wireOp",EDGE,"E98.MirrorCS");Q0=makeQuery(id+"F16.imprint","IMPRINT",FACE,{"disambiguationData":[TD([[makeQuery(id+"F16.imprint","IMPRINT",EDGE,{"derivedFrom":subQ1}),1.0]])]});}
            var Q1;
            {var subQ10=sQuery(id+"F16.wireOp",EDGE,"E81");Q1=makeQuery(id+"F16.imprint","IMPRINT",FACE,{"disambiguationData":[TD([[makeQuery(id+"F16.imprint","IMPRINT",EDGE,{"derivedFrom":subQ10}),-1.0]])]});}
            var Q2;
            Q2=makeQuery(id+"F16.imprint","IMPRINT",FACE,{"disambiguationData":[TD([[makeQuery(id+"F16.imprint","IMPRINT",EDGE,{"derivedFrom":makeQuery(id+"F1.opExtrude","CAP_EDGE",EDGE,{"disambiguationData":[OSD([sQuery(id+"F0.wireOp",EDGE,"E1.left")])],"isStart":true})}),-1.0]])]});
            var Q3;
            Q3=makeQuery(id+"F2.opExtrude","CAP_FACE",FACE,{"disambiguationData":[OSD([sQuery(id+"F0.wireOp",EDGE,"E12"),sQuery(id+"F0.wireOp",EDGE,"E13"),sQuery(id+"F0.wireOp",EDGE,"E14"),sQuery(id+"F0.wireOp",EDGE,"E15"),sQuery(id+"F0.wireOp",EDGE,"E17.filletArc"),sQuery(id+"F0.wireOp",EDGE,"E18.filletArc"),sQuery(id+"F0.wireOp",EDGE,"E19.filletArc"),sQuery(id+"F0.wireOp",EDGE,"E20.filletArc"),sQuery(id+"F0.wireOp",EDGE,"E25.0"),sQuery(id+"F0.wireOp",EDGE,"E25.1"),sQuery(id+"F0.wireOp",EDGE,"E25.2"),sQuery(id+"F0.wireOp",EDGE,"E25.3"),sQuery(id+"F0.wireOp",EDGE,"E25.4"),sQuery(id+"F0.wireOp",EDGE,"E25.5"),sQuery(id+"F0.wireOp",EDGE,"E25.6"),sQuery(id+"F0.wireOp",EDGE,"E25.7")])],"isStart":false});
            extrude(context, id + "F17", {"entities" : qUnion([Q0, Q1, Q2]), "operationType" : NewBodyOperationType.ADD, "endBound" : BoundingType.UP_TO_SURFACE, "depth" : 25 * mm, "endBoundEntityFace" : qUnion([Q3]), "offsetDistance" : 25 * mm});
        }
    });
